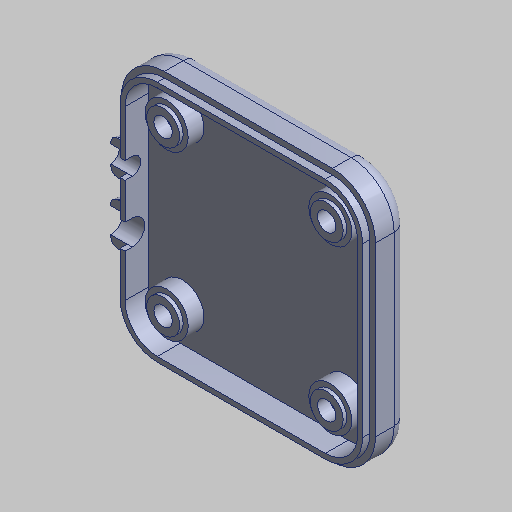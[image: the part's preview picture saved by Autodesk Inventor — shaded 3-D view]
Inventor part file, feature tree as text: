
AUTODESK INVENTOR PART (.ipt)
format: ipt  version: 2023.5 (Build 275446000, 446)  size: 212,992 bytes
history: native  units: mm (DEFAULTED — no unit token found)
features: fillet x1
ambient origin geometry x8: Origin, YZ Plane, XZ Plane, XY Plane, X Axis, Y Axis, Z Axis, Center Point
bodies: Solid1 (feature_tree)
feature tree (1):
  fillet  "Fillet5"  [1 undecoded]
note: 1 required parameter value undecoded (feature->parameter linkage not recoverable at this tier; creation-order binding heuristic only, values carry confidence <= 0.55)
